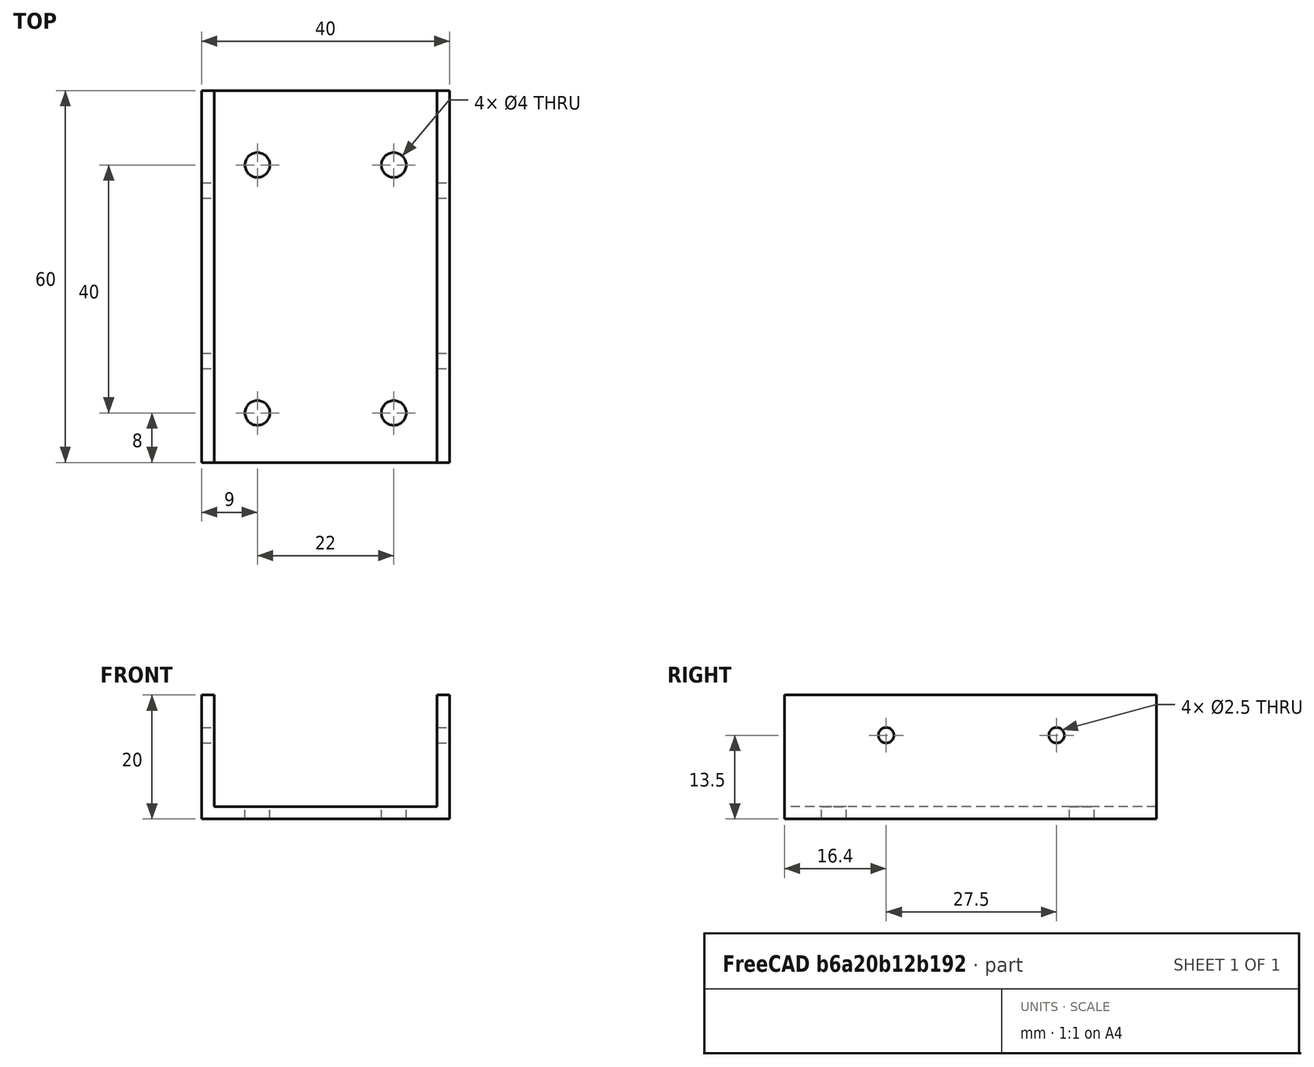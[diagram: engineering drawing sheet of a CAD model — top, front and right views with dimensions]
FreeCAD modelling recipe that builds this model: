
FCSTD DOCUMENT  (FreeCAD 0.15R4671 (Git))
Label: sujeccion inferior aluminio
License: All rights reserved
LicenseURL: http://es.wikipedia.org/wiki/Todos_los_derechos_reservados
objects: App::MeasureDistance×4, Part::Box×3, Part::Cut×3, Part::Cylinder×2, Part::FeaturePython×2, Part::MultiFuse×1
note: 11 computed .brp shape members not serialized (recipe doc carries the construction recipe); baked Part::Feature solids carry a one-line shape summary decoded from their .brp

FEATURE [Part::Box] Box  label="Cubo"
  Height = 2
  Length = 40
  Width = 60
FEATURE [Part::Box] Box001  label="Cubo001"
  Height = 20
  Length = 2
  Width = 60
FEATURE [Part::Cylinder] Cylinder  label="Cilindro"
  Angle = 360
  Height = 2
  Placement = pos=(0,16.4,13.5) rot=(0,1,0;1.5708rad)
  Radius = 1.25
FEATURE [Part::FeaturePython] Array  # Draft array (typed FeaturePython)
  Angle = 360
  ArrayType = 0
  Axis = (0,0,1)
  Base = -> Cylinder
  Center = (0,0,0)
  Fuse = false
  IntervalAxis = (0,0,0)
  IntervalX = (38,0,0)
  IntervalY = (0,27.5,0)
  IntervalZ = (0,0,0)
  NumberPolar = 1
  NumberX = 2
  NumberY = 2
  NumberZ = 1
  Placement = pos=(2,40,0) rot=(0,0,1;0rad)
FEATURE [Part::Box] Box002  label="Cubo002"
  Height = 20
  Length = 2
  Placement = pos=(38,0,0) rot=(0,0,1;0rad)
  Width = 60
FEATURE [Part::MultiFuse] Fusion
  Shapes = -> [Box002,Box001,Box]
FEATURE [Part::Cut] Cut
  Base = -> Fusion
  Placement = pos=(2,40,0) rot=(0,0,1;0rad)
  Tool = -> Array
FEATURE [Part::Cylinder] Cylinder001  label="Cilindro001"
  Angle = 360
  Height = 2
  Placement = pos=(11,48,0) rot=(0,0,1;0rad)
  Radius = 2
FEATURE [Part::FeaturePython] Array001  # Draft array (typed FeaturePython)
  Angle = 360
  ArrayType = 0
  Axis = (0,0,1)
  Base = -> Cylinder001
  Center = (0,0,0)
  Fuse = false
  IntervalAxis = (0,0,0)
  IntervalX = (22,0,0)
  IntervalY = (0,40,0)
  IntervalZ = (0,0,0)
  NumberPolar = 1
  NumberX = 2
  NumberY = 2
  NumberZ = 1
FEATURE [Part::Cut] Cut001
  Base = -> Cut
  Tool = -> Array001
FEATURE [App::MeasureDistance] Distance  label="Distance: 15.173"
  Distance = 15.1725
  P1 = (42,40,13.6285)
  P2 = (42,55.1721,13.7342)
FEATURE [App::MeasureDistance] Distance001  label="Distance: 17.660"
  Distance = 17.6604
  P1 = (42,57.6279,13.7342)
  P2 = (42,40,12.6618)
FEATURE [App::MeasureDistance] Distance002  label="Distance: 47.636"
  Distance = 47.6357
  P1 = (42,87.6279,13.7342)
  P2 = (42,40,12.8675)
FEATURE [App::MeasureDistance] Distance003  label="Distance: 45.065"
  Distance = 45.0653
  P1 = (42,40,12.8128)
  P2 = (42,85.0608,13.4507)
FEATURE [Part::Cut] Cut002
  Base = -> Cut001
  Tool = -> Array
